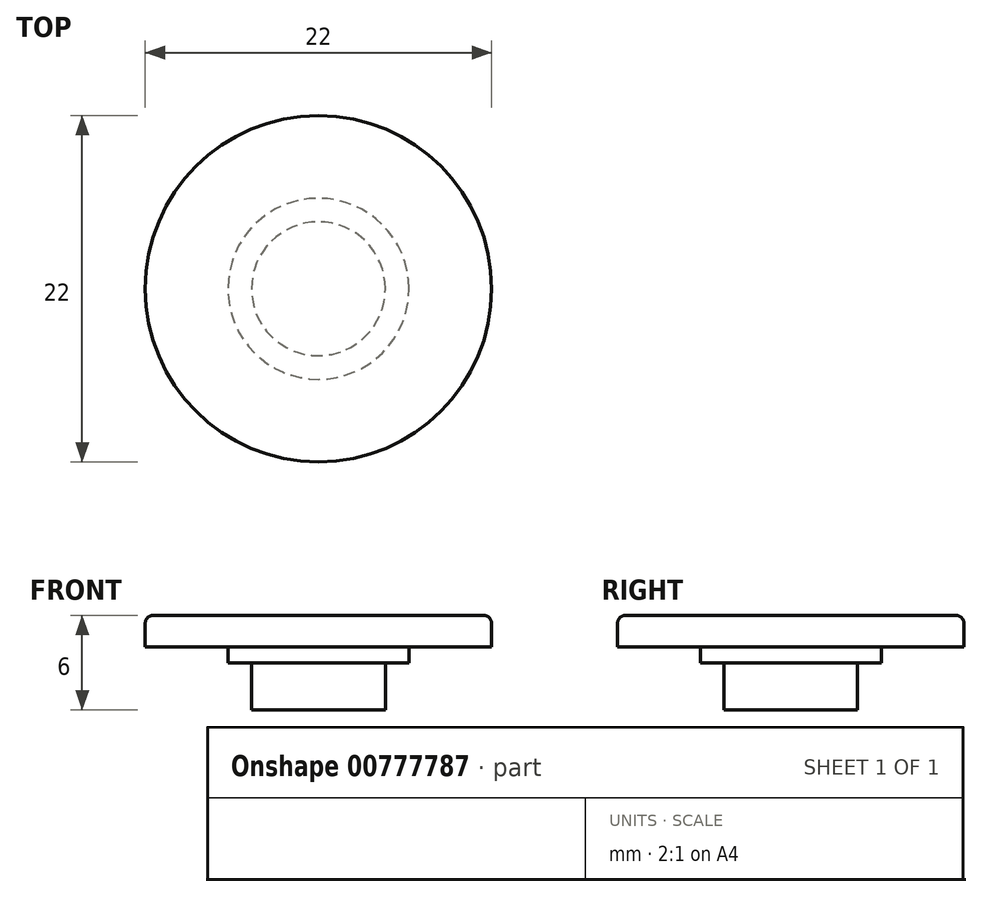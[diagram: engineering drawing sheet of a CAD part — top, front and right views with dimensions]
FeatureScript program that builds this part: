
annotation { "Feature Type Name" : "Feature", "Feature Type Description" : "" }
export const myFeature = defineFeature(function(context is Context, id is Id, definition is map)
    precondition{}
    {
        {
            var Q0;
            Q0=qCreatedBy(makeId("Top.planeOp"),FACE);
            var sketch = newSketch(context, id + "F0", { "sketchPlane" : qUnion([Q0])});
            skCircle(sketch, "E0", {"center": v(0, 0) * mm, "radius": 4.25 * mm});
            skSolve(sketch);
        }
        {
            var Q0;
            Q0 = qSketchRegion(id + "F0", true);
            extrude(context, id + "F1", {"entities" : qUnion([Q0]), "depth" : 3 * mm, "offsetDistance" : 25 * mm});
        }
        {
            var Q0;
            Q0=makeQuery(id+"F1.opExtrude","CAP_FACE",FACE,{"disambiguationData":[OSD([sQuery(id+"F0.wireOp",EDGE,"E0")])],"isStart":false});
            var sketch = newSketch(context, id + "F2", { "sketchPlane" : qUnion([Q0])});
            skCircle(sketch, "E1", {"center": v(0, 0) * mm, "radius": 5.75 * mm});
            skSolve(sketch);
        }
        {
            var Q0;
            Q0 = qSketchRegion(id + "F2", true);
            extrude(context, id + "F3", {"entities" : qUnion([Q0]), "operationType" : NewBodyOperationType.ADD, "depth" : 1 * mm, "offsetDistance" : 25 * mm});
        }
        {
            var Q0;
            Q0=makeQuery(id+"F3.opExtrude","CAP_FACE",FACE,{"disambiguationData":[OSD([sQuery(id+"F2.wireOp",EDGE,"E1")])],"isStart":false});
            var sketch = newSketch(context, id + "F4", { "sketchPlane" : qUnion([Q0])});
            skCircle(sketch, "E2", {"center": v(0, 0) * mm, "radius": 11 * mm});
            skSolve(sketch);
        }
        {
            var Q0;
            Q0 = qSketchRegion(id + "F4", true);
            extrude(context, id + "F5", {"entities" : qUnion([Q0]), "operationType" : NewBodyOperationType.ADD, "depth" : 2 * mm, "offsetDistance" : 25 * mm});
        }
        {
            var Q0;
            Q0=makeQuery(id+"F5.opExtrude","CAP_EDGE",EDGE,{"disambiguationData":[OSD([sQuery(id+"F4.wireOp",EDGE,"E2")])],"isStart":false});
            fillet(context, id + "F6", {"entities" : qUnion([Q0]), "radius" : .5 * mm, "tangentPropagation" : true, "allowEdgeOverflow" : false});
        }
    });
